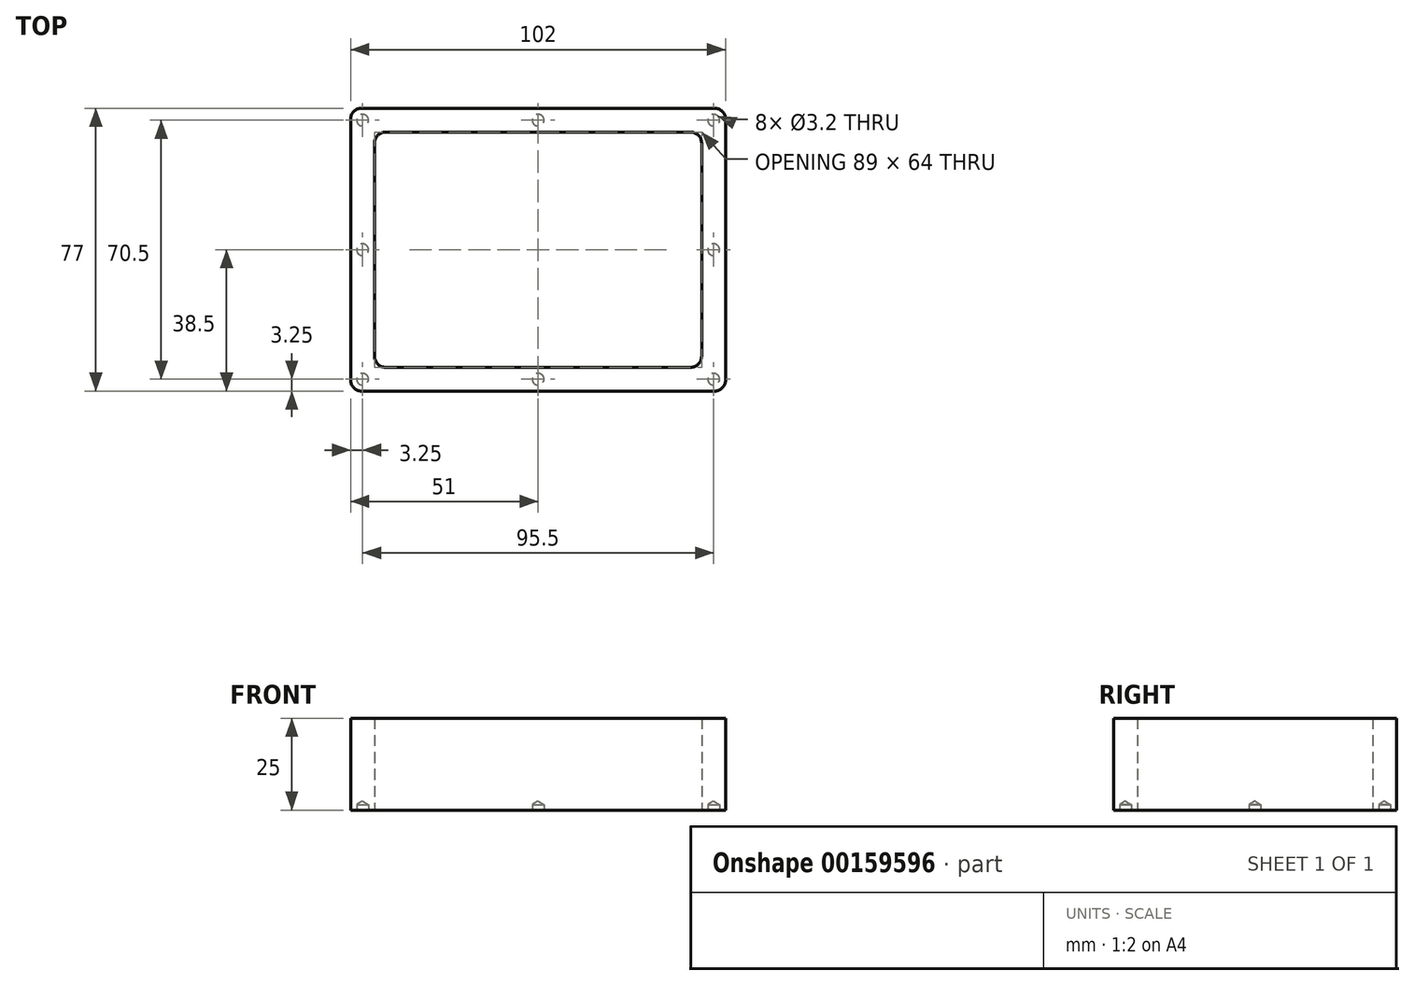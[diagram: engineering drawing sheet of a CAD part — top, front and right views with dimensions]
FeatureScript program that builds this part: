
annotation { "Feature Type Name" : "Feature", "Feature Type Description" : "" }
export const myFeature = defineFeature(function(context is Context, id is Id, definition is map)
    precondition{}
    {
        {
            var Q0;
            Q0=qCreatedBy(makeId("Top.planeOp"),FACE);
            var sketch = newSketch(context, id + "F0", { "sketchPlane" : qUnion([Q0])});
            skLineSegment(sketch, "E0.bottom", {"start": v(-32.5, 20) * mm, "end": v(32.5, 20) * mm});
            skLineSegment(sketch, "E0.top", {"start": v(-32.5, -20) * mm, "end": v(32.5, -20) * mm});
            skLineSegment(sketch, "E0.left", {"start": v(-32.5, 20) * mm, "end": v(-32.5, -20) * mm});
            skLineSegment(sketch, "E0.right", {"start": v(32.5, 20) * mm, "end": v(32.5, -20) * mm});
            skPoint(sketch, "E0.middle", {"position": v(0, 0) * mm});
            skLineSegment(sketch, "E1.0", {"start": v(-44.5, 32) * mm, "end": v(44.5, 32) * mm});
            skLineSegment(sketch, "E1.1", {"start": v(-44.5, 32) * mm, "end": v(-44.5, -32) * mm});
            skLineSegment(sketch, "E1.2", {"start": v(-44.5, -32) * mm, "end": v(44.5, -32) * mm});
            skLineSegment(sketch, "E1.3", {"start": v(44.5, 32) * mm, "end": v(44.5, -32) * mm});
            skLineSegment(sketch, "E2.0", {"start": v(-51, 38.5) * mm, "end": v(51, 38.5) * mm});
            skLineSegment(sketch, "E2.1", {"start": v(-51, 38.5) * mm, "end": v(-51, -38.5) * mm});
            skLineSegment(sketch, "E2.2", {"start": v(-51, -38.5) * mm, "end": v(51, -38.5) * mm});
            skLineSegment(sketch, "E2.3", {"start": v(51, 38.5) * mm, "end": v(51, -38.5) * mm});
            skLineSegment(sketch, "E3.0", {"start": v(-47.75, 35.25) * mm, "end": v(47.75, 35.25) * mm, "construction": true});
            skLineSegment(sketch, "E3.1", {"start": v(-47.75, 35.25) * mm, "end": v(-47.75, -35.25) * mm, "construction": true});
            skLineSegment(sketch, "E3.2", {"start": v(-47.75, -35.25) * mm, "end": v(47.75, -35.25) * mm, "construction": true});
            skLineSegment(sketch, "E3.3", {"start": v(47.75, 35.25) * mm, "end": v(47.75, -35.25) * mm, "construction": true});
            skPoint(sketch, "E4", {"position": v(-47.75, 0) * mm});
            skPoint(sketch, "E5", {"position": v(47.75, 0) * mm});
            skPoint(sketch, "E6", {"position": v(0, -35.25) * mm});
            skPoint(sketch, "E7", {"position": v(0, 35.25) * mm});
            skSolve(sketch);
        }
        {
            var Q0;
            Q0=makeQuery(id+"F0.imprint","IMPRINT",FACE,{"disambiguationData":[TD([[makeQuery(id+"F0.imprint","IMPRINT",EDGE,{"derivedFrom":sQuery(id+"F0.wireOp",EDGE,"E1.0")}),1.0]])]});
            extrude(context, id + "F1", {"entities" : qUnion([Q0]), "depth" : 25 * mm});
        }
        {
            var Q0;
            Q0=sQuery(id+"F0.wireOp",VERTEX,"E3.1.end");
            var Q1;
            Q1=sQuery(id+"F0.wireOp",VERTEX,"E6");
            var Q2;
            Q2=sQuery(id+"F0.wireOp",VERTEX,"E3.2.end");
            var Q3;
            Q3=sQuery(id+"F0.wireOp",VERTEX,"E5");
            var Q4;
            Q4=sQuery(id+"F0.wireOp",VERTEX,"E3.0.end");
            var Q5;
            Q5=sQuery(id+"F0.wireOp",VERTEX,"E7");
            var Q6;
            Q6=sQuery(id+"F0.wireOp",VERTEX,"E3.0.start");
            var Q7;
            Q7=sQuery(id+"F0.wireOp",VERTEX,"E4");
            var Q8;
            Q8=makeQuery(id+"F1.opExtrude","SWEPT_BODY",BODY,{"disambiguationData":[OSD([sQuery(id+"F0.wireOp",EDGE,"E1.0"),sQuery(id+"F0.wireOp",EDGE,"E1.1"),sQuery(id+"F0.wireOp",EDGE,"E1.2"),sQuery(id+"F0.wireOp",EDGE,"E1.3"),sQuery(id+"F0.wireOp",EDGE,"E2.0"),sQuery(id+"F0.wireOp",EDGE,"E2.1"),sQuery(id+"F0.wireOp",EDGE,"E2.2"),sQuery(id+"F0.wireOp",EDGE,"E2.3")])]});
            hole(context, id + "F2", {"style" : HoleStyle.SIMPLE, "endStyle" : HoleEndStyle.BLIND, "oppositeDirection" : true, "holeDiameter" : 3.2 * mm, "holeDepth" : 1.5 * mm, "locations" : qUnion([Q0, Q1, Q2, Q3, Q4, Q5, Q6, Q7]), "scope" : qUnion([Q8])});
        }
        {
            var Q0;
            Q0=makeQuery(id+"F1.opExtrude","SWEPT_EDGE",EDGE,{"disambiguationData":[OSD([sQuery(id+"F0.wireOp",EDGE,"E1.1"),sQuery(id+"F0.wireOp",EDGE,"E1.2")])]});
            var Q1;
            Q1=makeQuery(id+"F1.opExtrude","SWEPT_EDGE",EDGE,{"disambiguationData":[OSD([sQuery(id+"F0.wireOp",EDGE,"E1.2"),sQuery(id+"F0.wireOp",EDGE,"E1.3")])]});
            var Q2;
            Q2=makeQuery(id+"F1.opExtrude","SWEPT_EDGE",EDGE,{"disambiguationData":[OSD([sQuery(id+"F0.wireOp",EDGE,"E1.0"),sQuery(id+"F0.wireOp",EDGE,"E1.1")])]});
            var Q3;
            Q3=makeQuery(id+"F1.opExtrude","SWEPT_EDGE",EDGE,{"disambiguationData":[OSD([sQuery(id+"F0.wireOp",EDGE,"E1.0"),sQuery(id+"F0.wireOp",EDGE,"E1.3")])]});
            var Q4;
            Q4=makeQuery(id+"F1.opExtrude","SWEPT_EDGE",EDGE,{"disambiguationData":[OSD([sQuery(id+"F0.wireOp",EDGE,"E2.1"),sQuery(id+"F0.wireOp",EDGE,"E2.2")])]});
            var Q5;
            Q5=makeQuery(id+"F1.opExtrude","SWEPT_EDGE",EDGE,{"disambiguationData":[OSD([sQuery(id+"F0.wireOp",EDGE,"E2.0"),sQuery(id+"F0.wireOp",EDGE,"E2.1")])]});
            var Q6;
            Q6=makeQuery(id+"F1.opExtrude","SWEPT_EDGE",EDGE,{"disambiguationData":[OSD([sQuery(id+"F0.wireOp",EDGE,"E2.0"),sQuery(id+"F0.wireOp",EDGE,"E2.3")])]});
            var Q7;
            Q7=makeQuery(id+"F1.opExtrude","SWEPT_EDGE",EDGE,{"disambiguationData":[OSD([sQuery(id+"F0.wireOp",EDGE,"E2.2"),sQuery(id+"F0.wireOp",EDGE,"E2.3")])]});
            fillet(context, id + "F3", {"entities" : qUnion([Q0, Q1, Q2, Q3, Q4, Q5, Q6, Q7]), "radius" : 3 * mm, "tangentPropagation" : true, "allowEdgeOverflow" : false});
        }
    });
